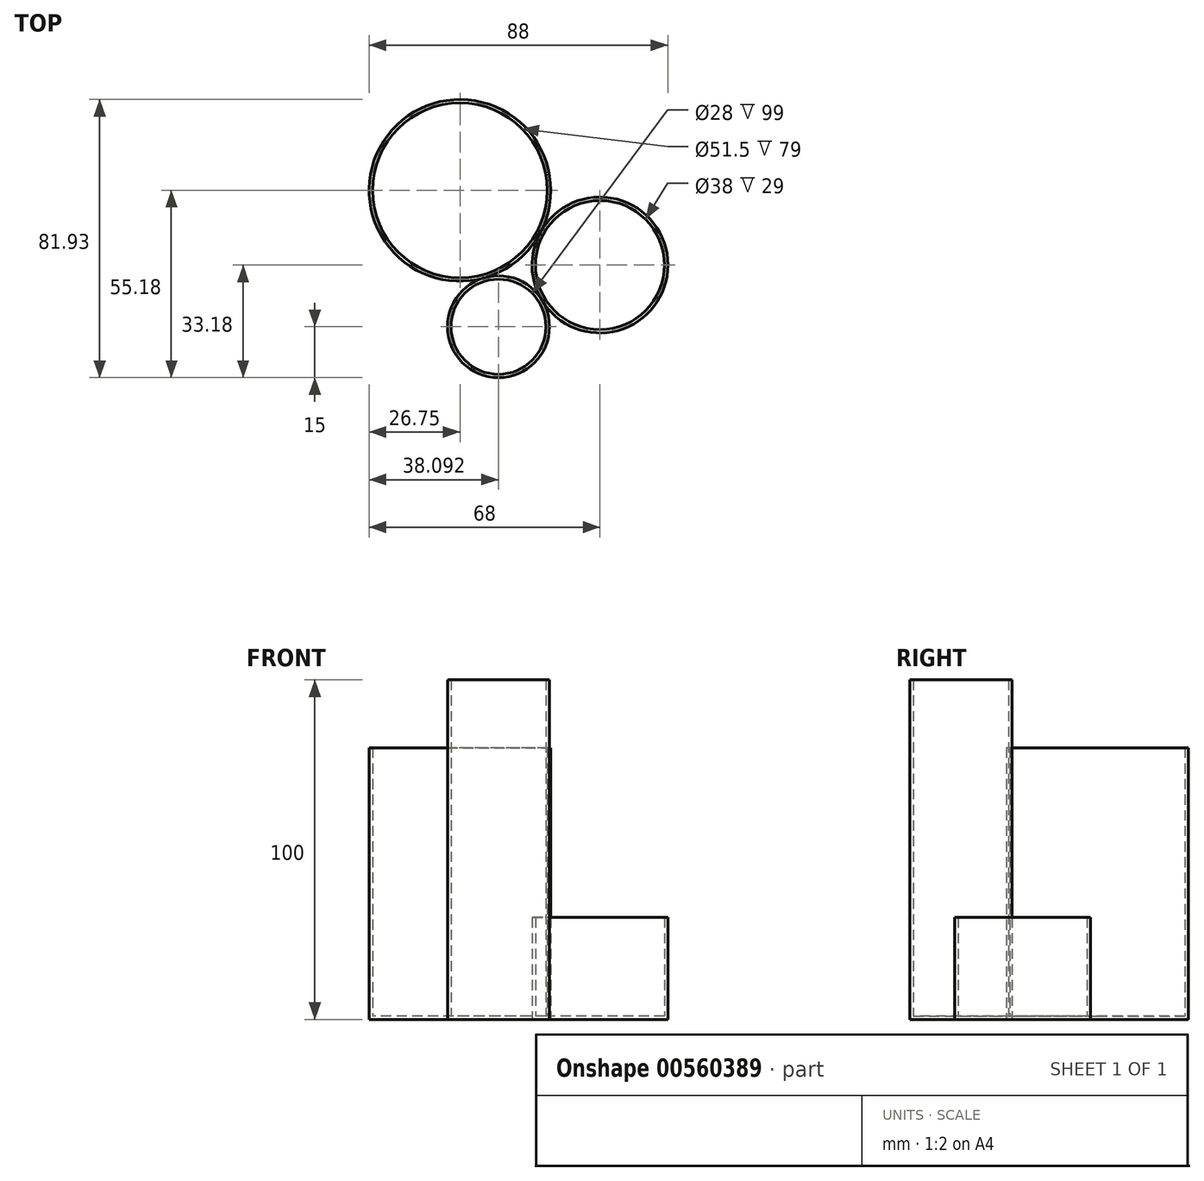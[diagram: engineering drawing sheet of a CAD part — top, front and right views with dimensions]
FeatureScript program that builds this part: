
annotation { "Feature Type Name" : "Feature", "Feature Type Description" : "" }
export const myFeature = defineFeature(function(context is Context, id is Id, definition is map)
    precondition{}
    {
        {
            var Q0;
            Q0=qCreatedBy(makeId("Top.planeOp"),FACE);
            var sketch = newSketch(context, id + "F0", { "sketchPlane" : qUnion([Q0])});
            skCircle(sketch, "E0", {"center": v(0, 0) * mm, "radius": 20 * mm});
            skSolve(sketch);
        }
        {
            var Q0;
            Q0=makeQuery(id+"F0.imprint","IMPRINT",FACE,{"disambiguationData":[TD([[makeQuery(id+"F0.imprint","IMPRINT",EDGE,{"derivedFrom":sQuery(id+"F0.wireOp",EDGE,"E0")}),1.0]])]});
            extrude(context, id + "F1", {"entities" : qUnion([Q0]), "depth" : 30 * mm, "offsetDistance" : 25 * mm});
        }
        {
            var Q0;
            Q0=makeQuery(id+"F1.opExtrude","CAP_FACE",FACE,{"disambiguationData":[OSD([sQuery(id+"F0.wireOp",EDGE,"E0")])],"isStart":false});
            shell(context, id + "F2", {"entities" : qUnion([Q0]), "thickness" : 1 * mm});
        }
        {
            var Q0;
            Q0=qCreatedBy(makeId("Top.planeOp"),FACE);
            var sketch = newSketch(context, id + "F3", { "sketchPlane" : qUnion([Q0])});
            skCircle(sketch, "E1", {"center": v(-41.25, 22) * mm, "radius": 26.75 * mm});
            skSolve(sketch);
        }
        {
            var Q0;
            Q0=makeQuery(id+"F3.imprint","IMPRINT",FACE,{"disambiguationData":[TD([[makeQuery(id+"F3.imprint","IMPRINT",EDGE,{"derivedFrom":sQuery(id+"F3.wireOp",EDGE,"E1")}),1.0]])]});
            extrude(context, id + "F4", {"entities" : qUnion([Q0]), "operationType" : NewBodyOperationType.ADD, "depth" : 80 * mm, "offsetDistance" : 25 * mm});
        }
        {
            var Q0;
            Q0=makeQuery(id+"F4.opExtrude","CAP_FACE",FACE,{"disambiguationData":[OSD([sQuery(id+"F3.wireOp",EDGE,"E1")])],"isStart":false});
            shell(context, id + "F5", {"entities" : qUnion([Q0]), "thickness" : 1 * mm});
        }
        {
            var Q0;
            Q0=qCreatedBy(makeId("Top.planeOp"),FACE);
            var sketch = newSketch(context, id + "F6", { "sketchPlane" : qUnion([Q0])});
            skCircle(sketch, "E2", {"center": v(-29.9, -18.18) * mm, "radius": 15 * mm});
            skSolve(sketch);
        }
        {
            var Q0;
            Q0=makeQuery(id+"F6.imprint","IMPRINT",FACE,{"disambiguationData":[TD([[makeQuery(id+"F6.imprint","IMPRINT",EDGE,{"derivedFrom":sQuery(id+"F6.wireOp",EDGE,"E2")}),1.0]])]});
            extrude(context, id + "F7", {"entities" : qUnion([Q0]), "depth" : 100 * mm, "offsetDistance" : 25 * mm});
        }
        {
            var Q0;
            Q0=makeQuery(id+"F7.opExtrude","CAP_FACE",FACE,{"disambiguationData":[OSD([sQuery(id+"F6.wireOp",EDGE,"E2")])],"isStart":false});
            shell(context, id + "F8", {"entities" : qUnion([Q0]), "thickness" : 1 * mm});
        }
    });
